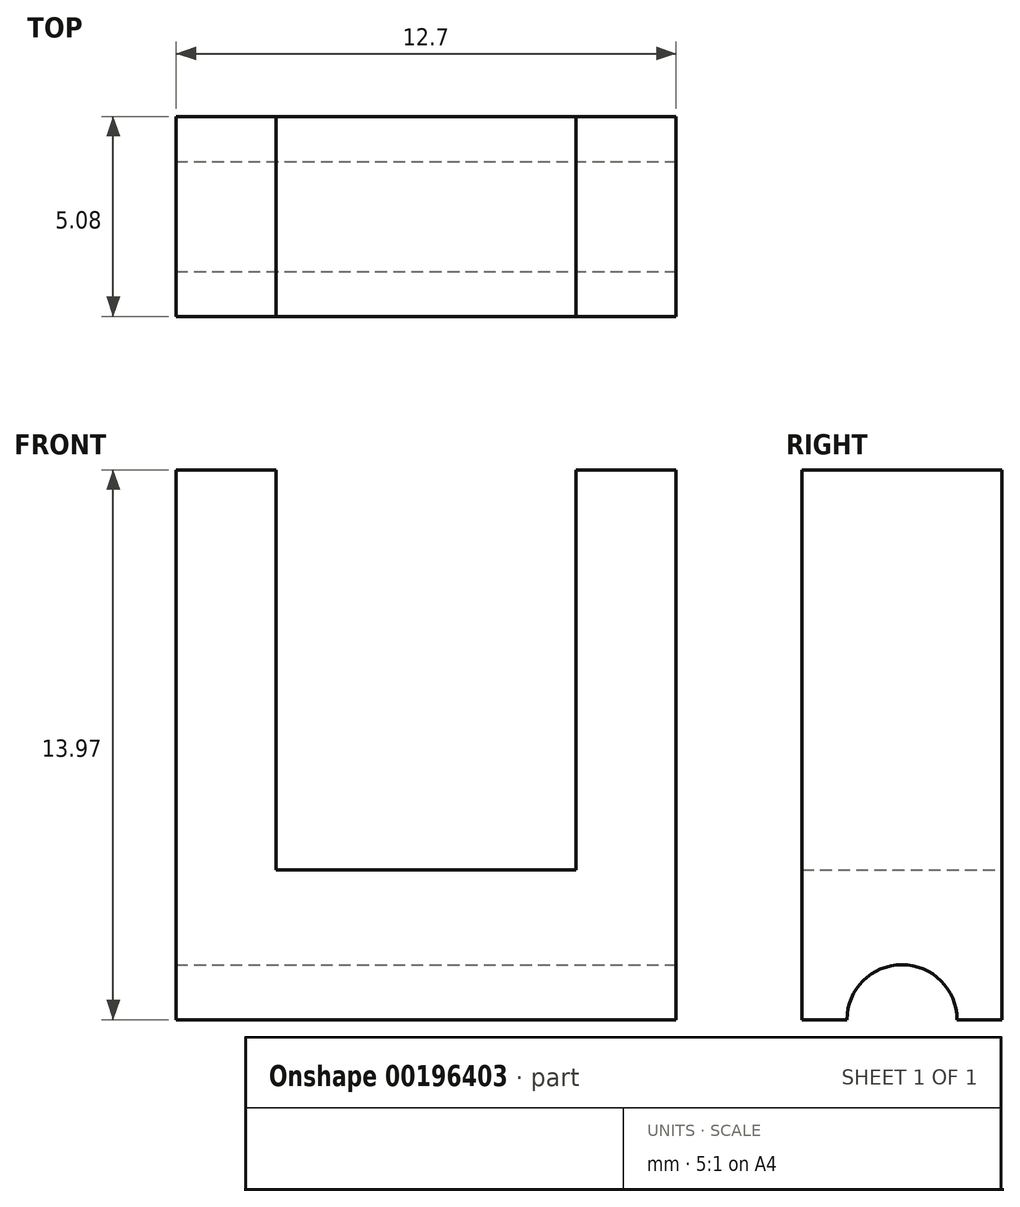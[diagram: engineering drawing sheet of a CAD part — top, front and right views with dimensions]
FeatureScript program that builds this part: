
annotation { "Feature Type Name" : "Feature", "Feature Type Description" : "" }
export const myFeature = defineFeature(function(context is Context, id is Id, definition is map)
    precondition{}
    {
        {
            var Q0;
            Q0=qCreatedBy(makeId("Front.planeOp"),FACE);
            var sketch = newSketch(context, id + "F0", { "sketchPlane" : qUnion([Q0])});
            skLineSegment(sketch, "E0", {"start": v(-18.37, 13.97) * mm, "end": v(-18.37, 0) * mm});
            skLineSegment(sketch, "E1", {"start": v(-18.37, 13.97) * mm, "end": v(-15.83, 13.97) * mm});
            skLineSegment(sketch, "E2", {"start": v(-15.83, 13.97) * mm, "end": v(-15.83, 3.81) * mm});
            skLineSegment(sketch, "E3", {"start": v(-15.83, 3.81) * mm, "end": v(-12.02, 3.81) * mm});
            skPoint(sketch, "E4", {"position": v(-12.02, 3.81) * mm});
            skPoint(sketch, "E5.orphan", {"position": v(-8.21, 3.81) * mm});
            skLineSegment(sketch, "E6", {"start": v(-12.02, 3.81) * mm, "end": v(-12.02, 0) * mm});
            skLineSegment(sketch, "E7.MirrorCS", {"start": v(-5.67, 13.97) * mm, "end": v(-5.67, 0) * mm});
            skLineSegment(sketch, "E8.MirrorCS", {"start": v(-8.21, 13.97) * mm, "end": v(-8.21, 3.81) * mm});
            skLineSegment(sketch, "E9.MirrorCS", {"start": v(-5.67, 13.97) * mm, "end": v(-8.21, 13.97) * mm});
            skLineSegment(sketch, "E10.MirrorCS", {"start": v(-8.21, 3.81) * mm, "end": v(-12.02, 3.81) * mm});
            skLineSegment(sketch, "E11", {"start": v(-18.37, 0) * mm, "end": v(-12.02, 0) * mm});
            skLineSegment(sketch, "E12.MirrorCS", {"start": v(-5.67, 0) * mm, "end": v(-12.02, 0) * mm});
            skSolve(sketch);
        }
        {
            var Q0;
            Q0=makeQuery(id+"F0.imprint","IMPRINT",FACE,{"disambiguationData":[TD([[makeQuery(id+"F0.imprint","IMPRINT",EDGE,{"derivedFrom":sQuery(id+"F0.wireOp",EDGE,"E0")}),1.0]])]});
            var Q1;
            Q1=makeQuery(id+"F0.imprint","IMPRINT",FACE,{"disambiguationData":[TD([[makeQuery(id+"F0.imprint","IMPRINT",EDGE,{"derivedFrom":sQuery(id+"F0.wireOp",EDGE,"E6")}),1.0]])]});
            extrude(context, id + "F1", {"entities" : qUnion([Q0, Q1]), "depth" : 5.08 * mm});
        }
        {
            var Q0;
            Q0=makeQuery(id+"F1.opExtrude","SWEPT_FACE",FACE,{"disambiguationData":[OSD([sQuery(id+"F0.wireOp",EDGE,"E7.MirrorCS")])]});
            var sketch = newSketch(context, id + "F2", { "sketchPlane" : qUnion([Q0])});
            skPoint(sketch, "E13", {"position": v(-2.54, 0) * mm});
            skCircle(sketch, "E14", {"center": v(-2.54, 0) * mm, "radius": 1.4 * mm});
            skSolve(sketch);
        }
        {
            var Q0;
            Q0 = qSketchRegion(id + "F2", true);
            extrude(context, id + "F3", {"entities" : qUnion([Q0]), "operationType" : NewBodyOperationType.REMOVE, "oppositeDirection" : true, "depth" : 25.4 * mm});
        }
    });
